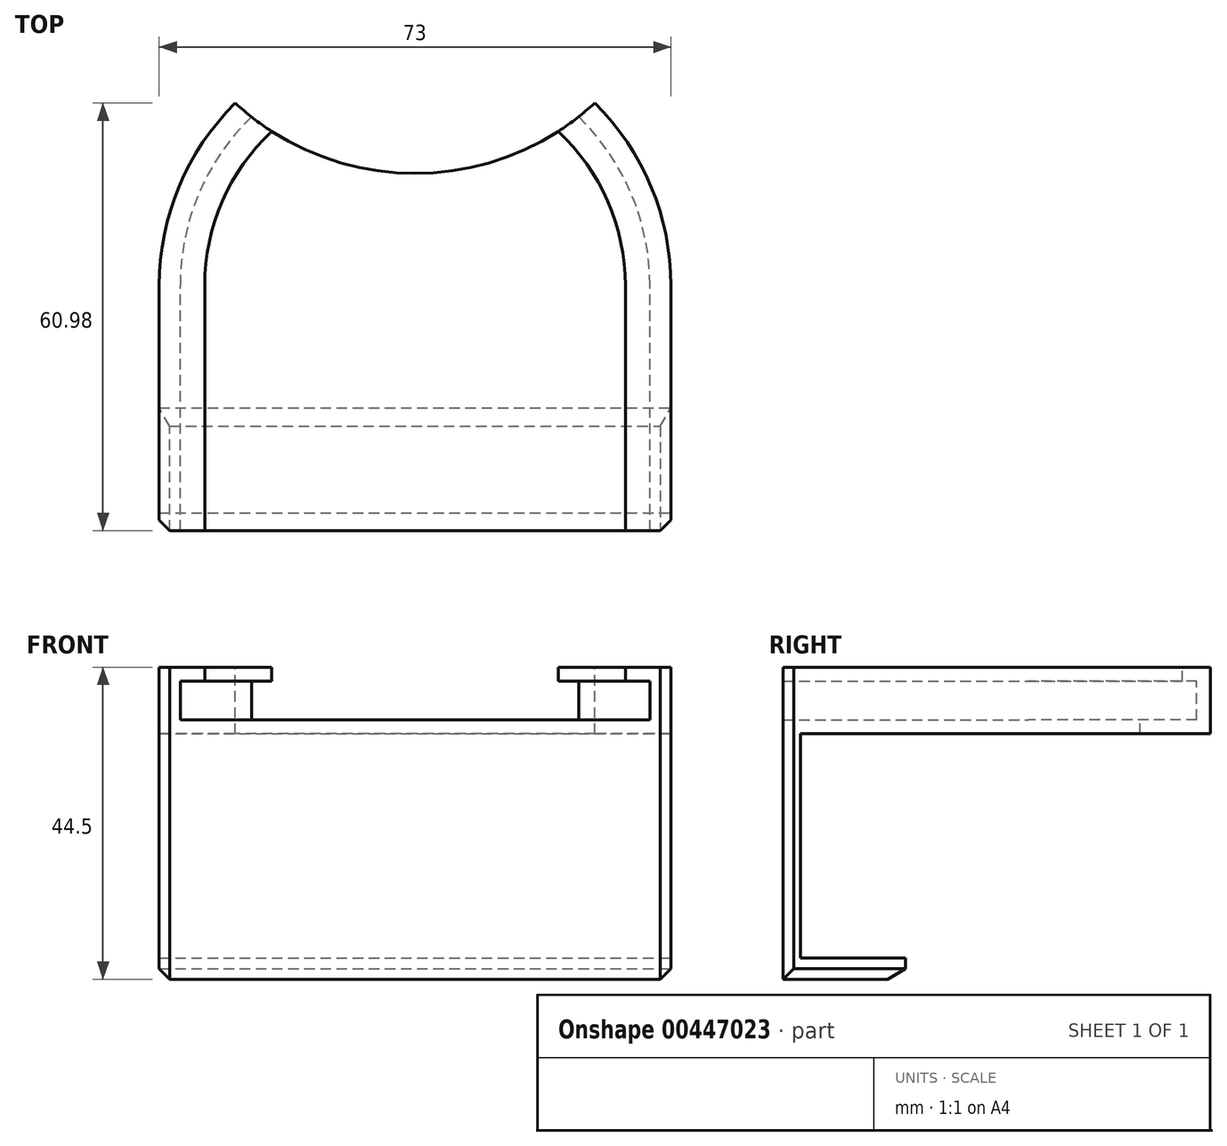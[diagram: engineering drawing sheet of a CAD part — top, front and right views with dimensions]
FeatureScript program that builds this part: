
annotation { "Feature Type Name" : "Feature", "Feature Type Description" : "" }
export const myFeature = defineFeature(function(context is Context, id is Id, definition is map)
    precondition{}
    {
        {
            var Q0;
            Q0=qCreatedBy(makeId("Front.planeOp"),FACE);
            var sketch = newSketch(context, id + "F0", { "sketchPlane" : qUnion([Q0])});
            skLineSegment(sketch, "E0", {"start": v(0, 34.15) * mm, "end": v(0, -30) * mm, "construction": true});
            skLineSegment(sketch, "E1", {"start": v(-33.5, 0) * mm, "end": v(-33.5, 5.5) * mm});
            skLineSegment(sketch, "E2", {"start": v(-33.5, 5.5) * mm, "end": v(-30, 5.5) * mm});
            skLineSegment(sketch, "E3", {"start": v(-30, 5.5) * mm, "end": v(-30, 7.5) * mm});
            skLineSegment(sketch, "E4", {"start": v(-30, 7.5) * mm, "end": v(-36.5, 7.5) * mm});
            skLineSegment(sketch, "E5", {"start": v(-36.5, 7.5) * mm, "end": v(-36.5, 0) * mm});
            skLineSegment(sketch, "E6", {"start": v(-36.5, 0) * mm, "end": v(-33.5, 0) * mm});
            skSolve(sketch);
        }
        {
            var Q0;
            Q0=makeQuery(id+"F0.imprint","IMPRINT",FACE,{"disambiguationData":[TD([[makeQuery(id+"F0.imprint","IMPRINT",EDGE,{"derivedFrom":sQuery(id+"F0.wireOp",EDGE,"E1")}),1.0]])]});
            var Q1;
            Q1 = qConstructionFilter(qBodyType(qCreatedBy(id + "F0" ,EDGE), BodyType.WIRE), ConstructionObject.NO);
            var Q2;
            Q2=sQuery(id+"F0.wireOp",EDGE,"E0");
            revolve(context, id + "F1", {"entities" : qUnion([Q0]), "surfaceEntities" : qUnion([Q1]), "axis" : qUnion([Q2]), "revolveType" : RevolveType.ONE_DIRECTION, "angle" : 180 * degree});
        }
        {
            var Q0;
            Q0=makeQuery(id+"F1.opRevolve","CAP_FACE",FACE,{"disambiguationData":[OSD([sQuery(id+"F0.wireOp",EDGE,"E1"),sQuery(id+"F0.wireOp",EDGE,"E2"),sQuery(id+"F0.wireOp",EDGE,"E3"),sQuery(id+"F0.wireOp",EDGE,"E4"),sQuery(id+"F0.wireOp",EDGE,"E5"),sQuery(id+"F0.wireOp",EDGE,"E6")])],"isStart":true});
            var Q1;
            Q1=makeQuery(id+"F1.opRevolve","CAP_FACE",FACE,{"disambiguationData":[OSD([sQuery(id+"F0.wireOp",EDGE,"E1"),sQuery(id+"F0.wireOp",EDGE,"E2"),sQuery(id+"F0.wireOp",EDGE,"E3"),sQuery(id+"F0.wireOp",EDGE,"E4"),sQuery(id+"F0.wireOp",EDGE,"E5"),sQuery(id+"F0.wireOp",EDGE,"E6")])],"isStart":false});
            extrude(context, id + "F2", {"entities" : qUnion([Q0, Q1]), "operationType" : NewBodyOperationType.ADD, "depth" : 35 * mm});
        }
        {
            var Q0;
            {var subQ0=sQuery(id+"F0.wireOp",EDGE,"E6");Q0=makeQuery(id+"F2.boolean.opBoolean","MERGE",FACE,{"derivedFrom":[makeQuery(id+"F1.opRevolve","SWEPT_FACE",FACE,{"disambiguationData":[OSD([subQ0])]}),makeQuery(id+"F2.opExtrude","SWEPT_FACE",FACE,{"disambiguationData":[OSD([subQ0]),TDD([makeQuery(id+"F1.opRevolve","CAP_EDGE",EDGE,{"disambiguationData":[OSD([subQ0])],"isStart":true})])]}),makeQuery(id+"F2.opExtrude","SWEPT_FACE",FACE,{"disambiguationData":[OSD([subQ0]),TDD([makeQuery(id+"F1.opRevolve","CAP_EDGE",EDGE,{"disambiguationData":[OSD([subQ0])],"isStart":false})])]})]});}
            var sketch = newSketch(context, id + "F3", { "sketchPlane" : qUnion([Q0])});
            skLineSegment(sketch, "E7.0", {"start": v(-36.5, 35) * mm, "end": v(-36.5, 0) * mm});
            skPoint(sketch, "E8.0", {"position": v(-35, 35) * mm});
            skPoint(sketch, "E9.0.end.orphan", {"position": v(-33.5, 35) * mm});
            skLineSegment(sketch, "E10.0", {"start": v(36.5, 35) * mm, "end": v(36.5, 0) * mm});
            skArc(sketch, "E11.0", {"start": v(36.5, 0) * mm, "mid": v(0, -36.5) * mm, "end": v(-36.5, 0) * mm});
            skLineSegment(sketch, "E12.0", {"start": v(-36.5, 35) * mm, "end": v(36.5, 35) * mm});
            skSolve(sketch);
        }
        {
            var Q0;
            Q0 = qSketchRegion(id + "F3", true);
            extrude(context, id + "F4", {"entities" : qUnion([Q0]), "operationType" : NewBodyOperationType.ADD, "depth" : 2 * mm});
        }
        {
            var Q0;
            Q0=qCreatedBy(makeId("Right.planeOp"),FACE);
            var sketch = newSketch(context, id + "F5", { "sketchPlane" : qUnion([Q0])});
            skLineSegment(sketch, "E13", {"start": v(-35, -2) * mm, "end": v(-35, -37) * mm});
            skLineSegment(sketch, "E14", {"start": v(-35, -37) * mm, "end": v(-20.1, -37) * mm});
            skLineSegment(sketch, "E15", {"start": v(-20.1, -37) * mm, "end": v(-17.5, -35.5) * mm});
            skLineSegment(sketch, "E16", {"start": v(-17.5, -35.5) * mm, "end": v(-17.5, -34) * mm});
            skLineSegment(sketch, "E17", {"start": v(-17.5, -34) * mm, "end": v(-32.5, -34) * mm});
            skLineSegment(sketch, "E18", {"start": v(-32.5, -34) * mm, "end": v(-32.5, -2) * mm});
            skLineSegment(sketch, "E19", {"start": v(-32.5, -2) * mm, "end": v(-35, -2) * mm});
            skSolve(sketch);
        }
        {
            var Q0;
            Q0=makeQuery(id+"F5.imprint","IMPRINT",FACE,{"disambiguationData":[TD([[makeQuery(id+"F5.imprint","IMPRINT",EDGE,{"derivedFrom":sQuery(id+"F5.wireOp",EDGE,"E13")}),1.0]])]});
            var Q1;
            Q1=makeQuery(id+"F4.opExtrude","SWEPT_FACE",FACE,{"disambiguationData":[OSD([sQuery(id+"F3.wireOp",EDGE,"E7.0")])]});
            var Q2;
            Q2=makeQuery(id+"F4.opExtrude","SWEPT_FACE",FACE,{"disambiguationData":[OSD([sQuery(id+"F3.wireOp",EDGE,"E10.0")])]});
            extrude(context, id + "F6", {"entities" : qUnion([Q0]), "operationType" : NewBodyOperationType.ADD, "endBound" : BoundingType.UP_TO_SURFACE, "oppositeDirection" : true, "endBoundEntityFace" : qUnion([Q1]), "depth" : 25 * mm, "hasSecondDirection" : true, "secondDirectionBound" : SecondDirectionBoundingType.UP_TO_SURFACE, "secondDirectionOppositeDirection" : false, "secondDirectionBoundEntityFace" : qUnion([Q2]), "secondDirectionDepth" : 25 * mm});
        }
        {
            var Q0;
            Q0=makeQuery(id+"F6.opExtrude","CAP_EDGE",EDGE,{"disambiguationData":[OSD([sQuery(id+"F5.wireOp",EDGE,"E14")])],"isStart":true});
            var Q1;
            Q1=makeQuery(id+"F6.opExtrude","CAP_EDGE",EDGE,{"disambiguationData":[OSD([sQuery(id+"F5.wireOp",EDGE,"E14")])],"isStart":false});
            var Q2;
            {var subQ0=sQuery(id+"F0.wireOp",EDGE,"E5");Q2=makeQuery(id+"F6.boolean.opBoolean","MERGE",EDGE,{"derivedFrom":[makeQuery(id+"F4.boolean.opBoolean","MERGE",EDGE,{"derivedFrom":[makeQuery(id+"F2.opExtrude","CAP_EDGE",EDGE,{"disambiguationData":[OSD([subQ0]),TDD([makeQuery(id+"F1.opRevolve","CAP_EDGE",EDGE,{"disambiguationData":[OSD([subQ0])],"isStart":false})])],"isStart":false}),makeQuery(id+"F4.opExtrude","SWEPT_EDGE",EDGE,{"disambiguationData":[OSD([sQuery(id+"F3.wireOp",EDGE,"E10.0"),sQuery(id+"F3.wireOp",EDGE,"E12.0")])]})]}),makeQuery(id+"F6.opExtrude","CAP_EDGE",EDGE,{"disambiguationData":[OSD([sQuery(id+"F5.wireOp",EDGE,"E13")])],"isStart":true})]});}
            var Q3;
            Q3=makeQuery(id+"F6.opExtrude","TWEAK_EDGE",EDGE,{"derivedFrom":[makeQuery(id+"F5.imprint","IMPRINT",EDGE,{"derivedFrom":sQuery(id+"F5.wireOp",EDGE,"E13")}),makeQuery(id+"F5.imprint","IMPRINT",EDGE,{"derivedFrom":sQuery(id+"F5.wireOp",EDGE,"E14")})]});
            var Q4;
            {var subQ0=sQuery(id+"F0.wireOp",EDGE,"E5");Q4=makeQuery(id+"F6.boolean.opBoolean","MERGE",EDGE,{"derivedFrom":[makeQuery(id+"F4.boolean.opBoolean","MERGE",EDGE,{"derivedFrom":[makeQuery(id+"F2.opExtrude","CAP_EDGE",EDGE,{"disambiguationData":[OSD([subQ0]),TDD([makeQuery(id+"F1.opRevolve","CAP_EDGE",EDGE,{"disambiguationData":[OSD([subQ0])],"isStart":true})])],"isStart":false}),makeQuery(id+"F4.opExtrude","SWEPT_EDGE",EDGE,{"disambiguationData":[OSD([sQuery(id+"F3.wireOp",EDGE,"E7.0"),sQuery(id+"F3.wireOp",EDGE,"E12.0")])]})]}),makeQuery(id+"F6.opExtrude","CAP_EDGE",EDGE,{"disambiguationData":[OSD([sQuery(id+"F5.wireOp",EDGE,"E13")])],"isStart":false})]});}
            chamfer(context, id + "F7", {"entities" : qUnion([Q0, Q1, Q2, Q3, Q4]), "width" : 1.5 * mm, "tangentPropagation" : true});
        }
        {
            var Q0;
            Q0=qCreatedBy(makeId("Top.planeOp"),FACE);
            var sketch = newSketch(context, id + "F8", { "sketchPlane" : qUnion([Q0])});
            skCircle(sketch, "E20", {"center": v(0, 53.73) * mm, "radius": 37.78 * mm});
            skSolve(sketch);
        }
        {
            var Q0;
            Q0=makeQuery(id+"F8.imprint","IMPRINT",FACE,{"disambiguationData":[TD([[makeQuery(id+"F8.imprint","IMPRINT",EDGE,{"derivedFrom":sQuery(id+"F8.wireOp",EDGE,"E20")}),1.0]])]});
            extrude(context, id + "F9", {"entities" : qUnion([Q0]), "operationType" : NewBodyOperationType.REMOVE, "endBound" : BoundingType.THROUGH_ALL, "oppositeDirection" : true, "depth" : 25 * mm, "hasSecondDirection" : true, "secondDirectionBound" : SecondDirectionBoundingType.THROUGH_ALL, "secondDirectionOppositeDirection" : false, "secondDirectionDepth" : 25 * mm});
        }
    });
